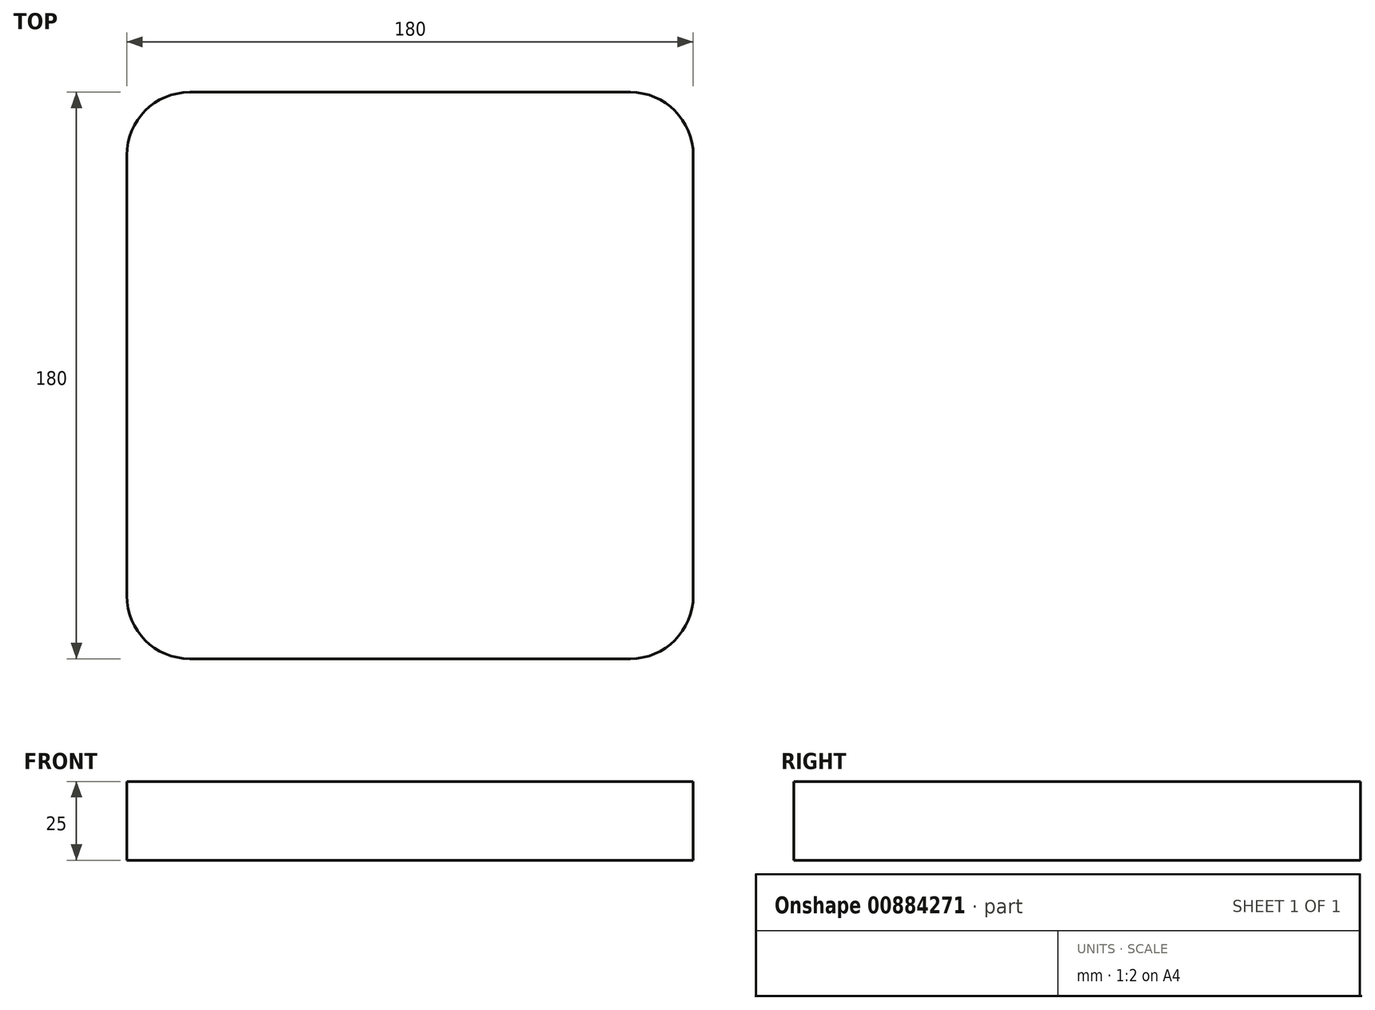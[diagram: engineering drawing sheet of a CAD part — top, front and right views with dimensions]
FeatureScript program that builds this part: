
annotation { "Feature Type Name" : "Feature", "Feature Type Description" : "" }
export const myFeature = defineFeature(function(context is Context, id is Id, definition is map)
    precondition{}
    {
        {
            var Q0;
            Q0=qCreatedBy(makeId("Top.planeOp"),FACE);
            var sketch = newSketch(context, id + "F0", { "sketchPlane" : qUnion([Q0])});
            skLineSegment(sketch, "E0.bottom", {"start": v(-90, 90) * mm, "end": v(90, 90) * mm});
            skLineSegment(sketch, "E0.top", {"start": v(-90, -90) * mm, "end": v(90, -90) * mm});
            skLineSegment(sketch, "E0.left", {"start": v(-90, 90) * mm, "end": v(-90, -90) * mm});
            skLineSegment(sketch, "E0.right", {"start": v(90, 90) * mm, "end": v(90, -90) * mm});
            skPoint(sketch, "E0.middle", {"position": v(0, 0) * mm});
            skSolve(sketch);
        }
        {
            var Q0;
            Q0=makeQuery(id+"F0.imprint","IMPRINT",FACE,{"disambiguationData":[TD([[makeQuery(id+"F0.imprint","IMPRINT",EDGE,{"derivedFrom":sQuery(id+"F0.wireOp",EDGE,"E0.bottom")}),-1.0]])]});
            extrude(context, id + "F1", {"entities" : qUnion([Q0]), "depth" : 25 * mm, "offsetDistance" : 25 * mm});
        }
        {
            var Q0;
            Q0=makeQuery(id+"F1.opExtrude","SWEPT_EDGE",EDGE,{"disambiguationData":[OSD([sQuery(id+"F0.wireOp",EDGE,"E0.top"),sQuery(id+"F0.wireOp",EDGE,"E0.left")])]});
            var Q1;
            Q1=makeQuery(id+"F1.opExtrude","SWEPT_EDGE",EDGE,{"disambiguationData":[OSD([sQuery(id+"F0.wireOp",EDGE,"E0.top"),sQuery(id+"F0.wireOp",EDGE,"E0.right")])]});
            var Q2;
            Q2=makeQuery(id+"F1.opExtrude","SWEPT_EDGE",EDGE,{"disambiguationData":[OSD([sQuery(id+"F0.wireOp",EDGE,"E0.bottom"),sQuery(id+"F0.wireOp",EDGE,"E0.right")])]});
            var Q3;
            Q3=makeQuery(id+"F1.opExtrude","SWEPT_EDGE",EDGE,{"disambiguationData":[OSD([sQuery(id+"F0.wireOp",EDGE,"E0.bottom"),sQuery(id+"F0.wireOp",EDGE,"E0.left")])]});
            fillet(context, id + "F2", {"entities" : qUnion([Q0, Q1, Q2, Q3]), "tangentPropagation" : true, "radius" : 20 * mm, "defaultsChanged" : true, "vertexSettings" : [], "allowEdgeOverflow" : false});
        }
    });
